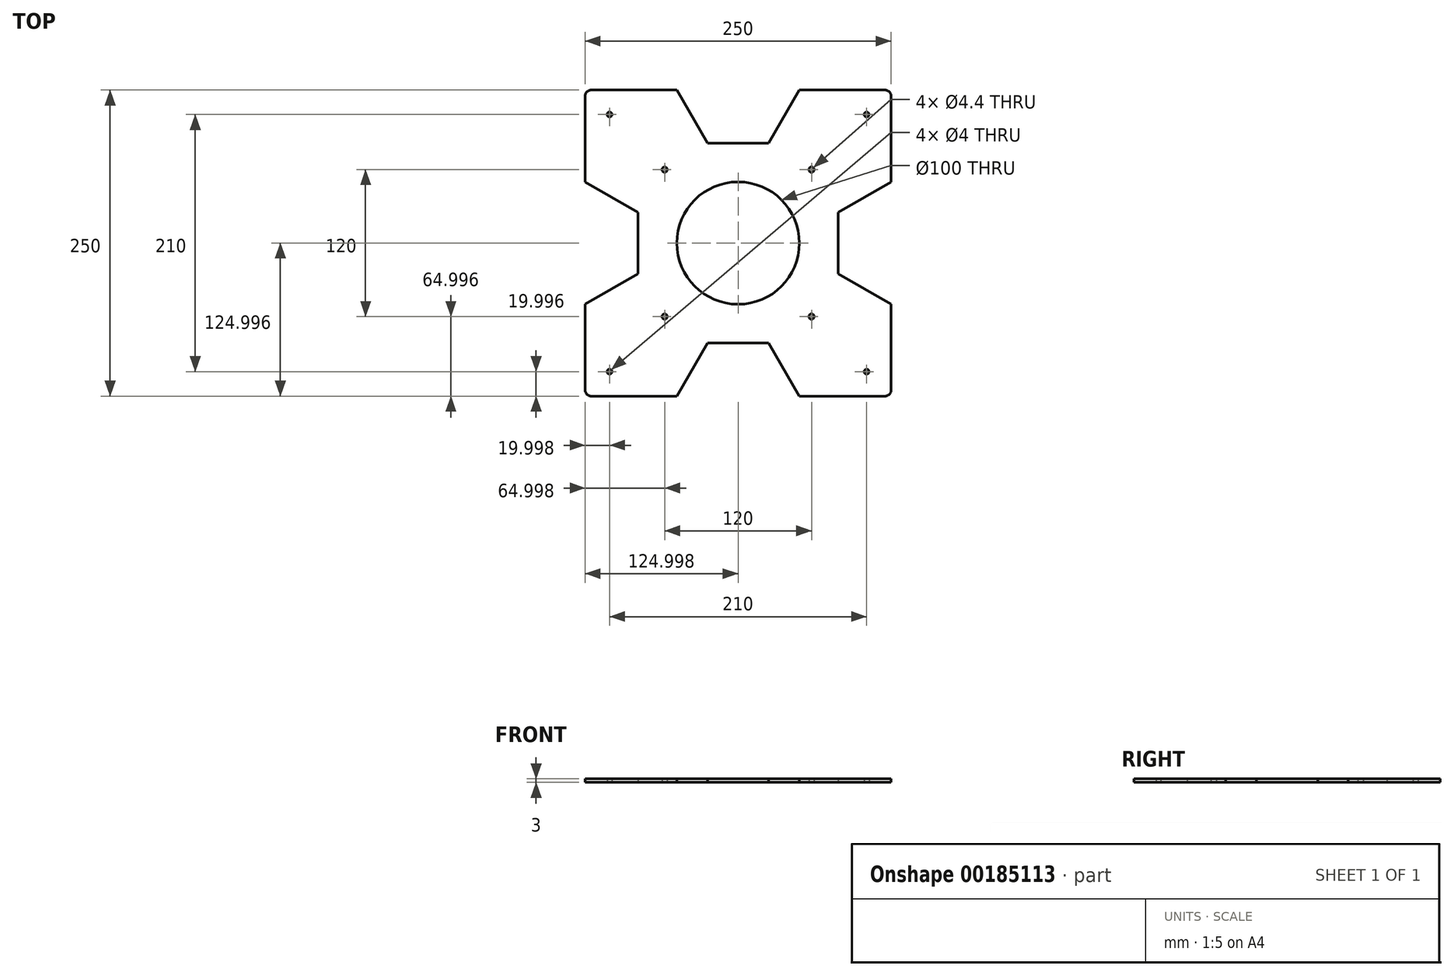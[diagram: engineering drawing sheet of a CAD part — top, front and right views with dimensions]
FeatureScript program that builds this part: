
annotation { "Feature Type Name" : "Feature", "Feature Type Description" : "" }
export const myFeature = defineFeature(function(context is Context, id is Id, definition is map)
    precondition{}
    {
        {
            var Q0;
            Q0=qCreatedBy(makeId("Top.planeOp"),FACE);
            var sketch = newSketch(context, id + "F0", { "sketchPlane" : qUnion([Q0])});
            skLineSegment(sketch, "E0.bottom", {"start": v(-171.8, 211.8) * mm, "end": v(-101.8, 211.8) * mm});
            skLineSegment(sketch, "E0.top", {"start": v(-171.8, -38.2) * mm, "end": v(-101.8, -38.2) * mm});
            skLineSegment(sketch, "E0.left", {"start": v(-176.8, 206.8) * mm, "end": v(-176.8, 136.8) * mm});
            skLineSegment(sketch, "E0.right", {"start": v(73.2, 206.8) * mm, "end": v(73.2, 136.8) * mm});
            skPoint(sketch, "E1", {"position": v(-111.8, 146.8) * mm});
            skPoint(sketch, "E2", {"position": v(8.2, 146.8) * mm});
            skPoint(sketch, "E3", {"position": v(8.2, 26.8) * mm});
            skPoint(sketch, "E4", {"position": v(-111.8, 26.8) * mm});
            skPoint(sketch, "E5", {"position": v(-156.8, 191.8) * mm});
            skPoint(sketch, "E6", {"position": v(53.2, 191.8) * mm});
            skPoint(sketch, "E7", {"position": v(53.2, -18.2) * mm});
            skPoint(sketch, "E8", {"position": v(-156.8, -18.2) * mm});
            skCircle(sketch, "E9", {"center": v(-51.8, 86.8) * mm, "radius": 50 * mm});
            skLineSegment(sketch, "E10.1", {"start": v(-176.8, 136.8) * mm, "end": v(-133.5, 111.8) * mm});
            skLineSegment(sketch, "E10.2", {"start": v(-133.5, 111.8) * mm, "end": v(-133.5, 61.8) * mm});
            skLineSegment(sketch, "E10.3", {"start": v(-133.5, 61.8) * mm, "end": v(-176.8, 36.8) * mm});
            skLineSegment(sketch, "E11.0", {"start": v(29.9, 111.8) * mm, "end": v(73.2, 136.8) * mm});
            skLineSegment(sketch, "E11.4", {"start": v(73.2, 36.8) * mm, "end": v(29.9, 61.8) * mm});
            skLineSegment(sketch, "E11.5", {"start": v(29.9, 61.8) * mm, "end": v(29.9, 111.8) * mm});
            skPoint(sketch, "E11.0.midPoint", {"position": v(51.56, 124.3) * mm});
            skPoint(sketch, "E12", {"position": v(-51.8, 211.8) * mm});
            skPoint(sketch, "E13", {"position": v(73.2, 86.8) * mm});
            skPoint(sketch, "E14", {"position": v(-51.8, -38.2) * mm});
            skLineSegment(sketch, "E15.3", {"start": v(-1.8, 211.8) * mm, "end": v(-26.8, 168.5) * mm});
            skLineSegment(sketch, "E15.4", {"start": v(-26.8, 168.5) * mm, "end": v(-76.8, 168.5) * mm});
            skLineSegment(sketch, "E15.5", {"start": v(-76.8, 168.5) * mm, "end": v(-101.8, 211.8) * mm});
            skLineSegment(sketch, "E16.0", {"start": v(-101.8, -38.2) * mm, "end": v(-76.8, 5.1) * mm});
            skLineSegment(sketch, "E16.1", {"start": v(-76.8, 5.1) * mm, "end": v(-26.8, 5.1) * mm});
            skLineSegment(sketch, "E16.2", {"start": v(-26.8, 5.1) * mm, "end": v(-1.8, -38.2) * mm});
            skPoint(sketch, "E10.cCircle.center.orphan", {"position": v(-176.8, 86.8) * mm});
            skLineSegment(sketch, "E17.trimOffspring", {"start": v(-176.8, 36.8) * mm, "end": v(-176.8, -33.2) * mm});
            skLineSegment(sketch, "E18.trimOffspring", {"start": v(-1.8, 211.8) * mm, "end": v(68.2, 211.8) * mm});
            skLineSegment(sketch, "E19.trimOffspring", {"start": v(73.2, 36.8) * mm, "end": v(73.2, -33.2) * mm});
            skLineSegment(sketch, "E20.trimOffspring", {"start": v(-1.8, -38.2) * mm, "end": v(68.2, -38.2) * mm});
            skPoint(sketch, "E21.visualSharp", {"position": v(-176.8, 211.8) * mm});
            skArc(sketch, "E21.filletArc", {"start": v(-171.8, 211.8) * mm, "mid": v(-175.33, 210.34) * mm, "end": v(-176.8, 206.8) * mm});
            skPoint(sketch, "E22.visualSharp", {"position": v(73.2, 211.8) * mm});
            skArc(sketch, "E22.filletArc", {"start": v(73.2, 206.8) * mm, "mid": v(71.74, 210.34) * mm, "end": v(68.2, 211.8) * mm});
            skPoint(sketch, "E23.visualSharp", {"position": v(73.2, -38.2) * mm});
            skArc(sketch, "E23.filletArc", {"start": v(68.2, -38.2) * mm, "mid": v(71.74, -36.73) * mm, "end": v(73.2, -33.2) * mm});
            skPoint(sketch, "E24.visualSharp", {"position": v(-176.8, -38.2) * mm});
            skArc(sketch, "E24.filletArc", {"start": v(-176.8, -33.2) * mm, "mid": v(-175.33, -36.73) * mm, "end": v(-171.8, -38.2) * mm});
            skSolve(sketch);
        }
        {
            var Q0;
            Q0=makeQuery(id+"F0.imprint","IMPRINT",FACE,{"disambiguationData":[TD([[makeQuery(id+"F0.imprint","IMPRINT",EDGE,{"derivedFrom":sQuery(id+"F0.wireOp",EDGE,"E0.bottom")}),-1.0]])]});
            extrude(context, id + "F1", {"entities" : qUnion([Q0]), "depth" : 3 * mm});
        }
        {
            var Q0;
            Q0=sQuery(id+"F0.wireOp",VERTEX,"E1");
            var Q1;
            Q1=sQuery(id+"F0.wireOp",VERTEX,"E4");
            var Q2;
            Q2=sQuery(id+"F0.wireOp",VERTEX,"E3");
            var Q3;
            Q3=sQuery(id+"F0.wireOp",VERTEX,"E2");
            var Q4;
            Q4=makeQuery(id+"F1.opExtrude","SWEPT_BODY",BODY,{"disambiguationData":[OSD([sQuery(id+"F0.wireOp",EDGE,"E0.bottom"),sQuery(id+"F0.wireOp",EDGE,"E0.top"),sQuery(id+"F0.wireOp",EDGE,"E0.left"),sQuery(id+"F0.wireOp",EDGE,"E0.right"),sQuery(id+"F0.wireOp",EDGE,"E9"),sQuery(id+"F0.wireOp",EDGE,"E10.1"),sQuery(id+"F0.wireOp",EDGE,"E10.2"),sQuery(id+"F0.wireOp",EDGE,"E10.3"),sQuery(id+"F0.wireOp",EDGE,"E11.0"),sQuery(id+"F0.wireOp",EDGE,"E11.4"),sQuery(id+"F0.wireOp",EDGE,"E11.5"),sQuery(id+"F0.wireOp",EDGE,"E15.3"),sQuery(id+"F0.wireOp",EDGE,"E15.4"),sQuery(id+"F0.wireOp",EDGE,"E15.5"),sQuery(id+"F0.wireOp",EDGE,"E16.0"),sQuery(id+"F0.wireOp",EDGE,"E16.1"),sQuery(id+"F0.wireOp",EDGE,"E16.2"),sQuery(id+"F0.wireOp",EDGE,"E17.trimOffspring"),sQuery(id+"F0.wireOp",EDGE,"E18.trimOffspring"),sQuery(id+"F0.wireOp",EDGE,"E19.trimOffspring"),sQuery(id+"F0.wireOp",EDGE,"E20.trimOffspring"),sQuery(id+"F0.wireOp",EDGE,"E21.filletArc"),sQuery(id+"F0.wireOp",EDGE,"E22.filletArc"),sQuery(id+"F0.wireOp",EDGE,"E23.filletArc"),sQuery(id+"F0.wireOp",EDGE,"E24.filletArc")])]});
            hole(context, id + "F2", {"style" : HoleStyle.SIMPLE, "endStyle" : HoleEndStyle.THROUGH, "oppositeDirection" : true, "standardTappedOrClearance" : lookupTablePath({ "standard" : "ISO", "engagement" : "25%", "pitch" : "0.9 mm", "size" : "M5", "type" : "Tapped" }), "standardBlindInLast" : lookupTablePath({ "standard" : "ISO", "engagement" : "25%", "pitch" : "0.9 mm", "size" : "M5", "type" : "Tapped" }), "holeDiameter" : 4.4 * mm, "locations" : qUnion([Q0, Q1, Q2, Q3]), "scope" : qUnion([Q4]), "isTappedThrough" : true, "showTappedDepth" : true});
        }
        {
            var Q0;
            Q0=sQuery(id+"F0.wireOp",VERTEX,"E5");
            var Q1;
            Q1=sQuery(id+"F0.wireOp",VERTEX,"E8");
            var Q2;
            Q2=sQuery(id+"F0.wireOp",VERTEX,"E7");
            var Q3;
            Q3=sQuery(id+"F0.wireOp",VERTEX,"E6");
            var Q4;
            Q4=makeQuery(id+"F1.opExtrude","SWEPT_BODY",BODY,{"disambiguationData":[OSD([sQuery(id+"F0.wireOp",EDGE,"E0.bottom"),sQuery(id+"F0.wireOp",EDGE,"E0.top"),sQuery(id+"F0.wireOp",EDGE,"E0.left"),sQuery(id+"F0.wireOp",EDGE,"E0.right"),sQuery(id+"F0.wireOp",EDGE,"E9"),sQuery(id+"F0.wireOp",EDGE,"E10.1"),sQuery(id+"F0.wireOp",EDGE,"E10.2"),sQuery(id+"F0.wireOp",EDGE,"E10.3"),sQuery(id+"F0.wireOp",EDGE,"E11.0"),sQuery(id+"F0.wireOp",EDGE,"E11.4"),sQuery(id+"F0.wireOp",EDGE,"E11.5"),sQuery(id+"F0.wireOp",EDGE,"E15.3"),sQuery(id+"F0.wireOp",EDGE,"E15.4"),sQuery(id+"F0.wireOp",EDGE,"E15.5"),sQuery(id+"F0.wireOp",EDGE,"E16.0"),sQuery(id+"F0.wireOp",EDGE,"E16.1"),sQuery(id+"F0.wireOp",EDGE,"E16.2"),sQuery(id+"F0.wireOp",EDGE,"E17.trimOffspring"),sQuery(id+"F0.wireOp",EDGE,"E18.trimOffspring"),sQuery(id+"F0.wireOp",EDGE,"E19.trimOffspring"),sQuery(id+"F0.wireOp",EDGE,"E20.trimOffspring"),sQuery(id+"F0.wireOp",EDGE,"E21.filletArc"),sQuery(id+"F0.wireOp",EDGE,"E22.filletArc"),sQuery(id+"F0.wireOp",EDGE,"E23.filletArc"),sQuery(id+"F0.wireOp",EDGE,"E24.filletArc")])]});
            hole(context, id + "F3", {"style" : HoleStyle.SIMPLE, "endStyle" : HoleEndStyle.THROUGH, "oppositeDirection" : true, "standardTappedOrClearance" : lookupTablePath({ "standard" : "ISO", "size" : "4", "type" : "Drilled" }), "standardBlindInLast" : lookupTablePath({ "standard" : "ISO", "size" : "4", "type" : "Drilled" }), "holeDiameter" : 4 * mm, "locations" : qUnion([Q0, Q1, Q2, Q3]), "scope" : qUnion([Q4]), "isTappedThrough" : true});
        }
    });
